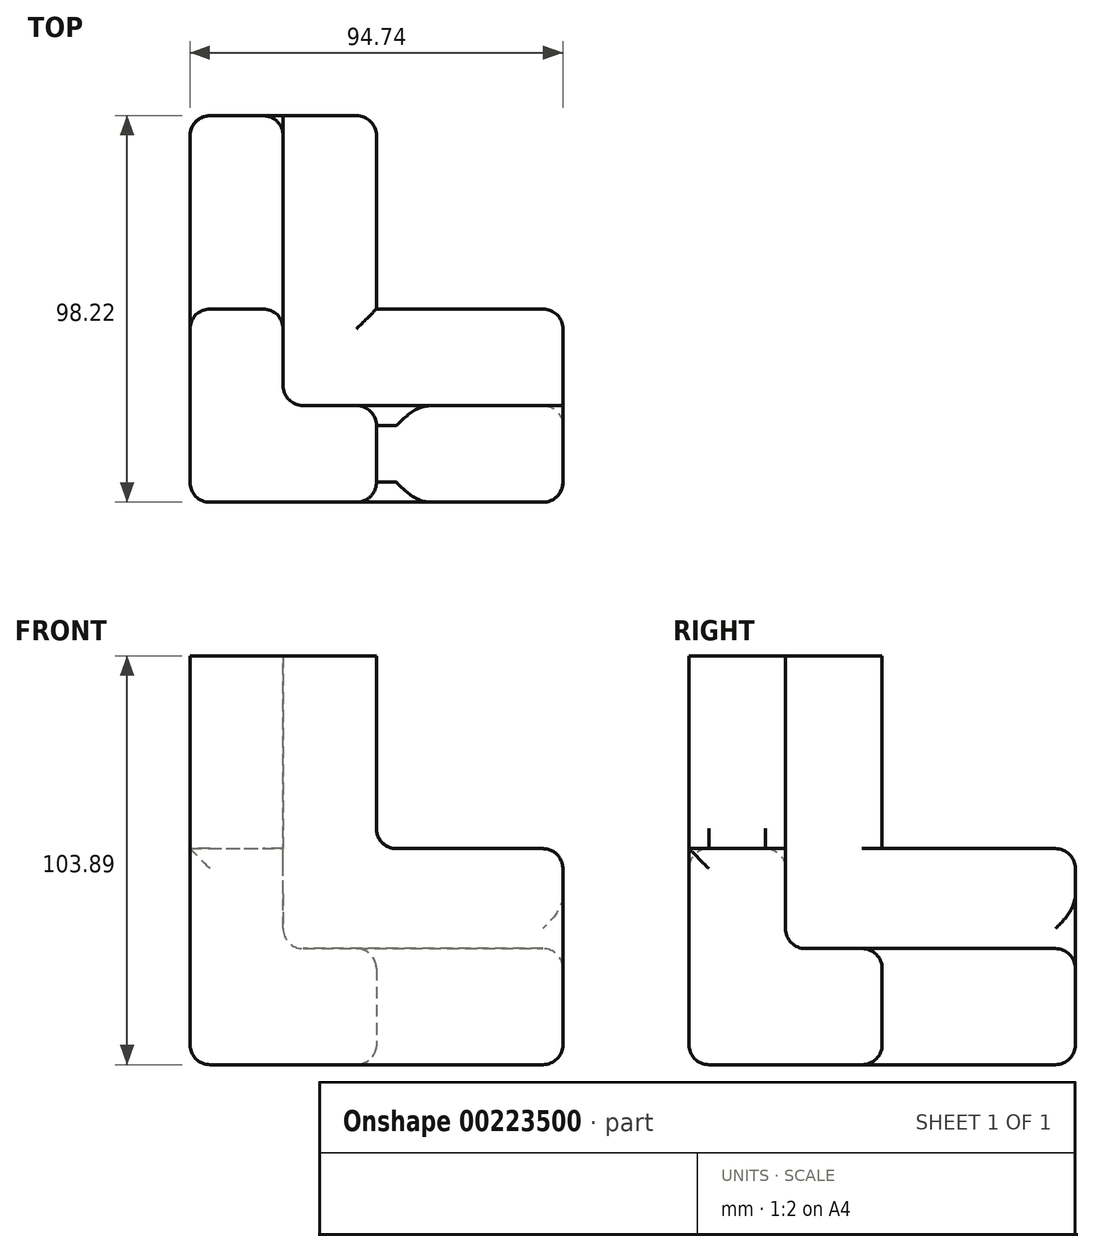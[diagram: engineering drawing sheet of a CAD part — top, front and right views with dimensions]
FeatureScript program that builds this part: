
annotation { "Feature Type Name" : "Feature", "Feature Type Description" : "" }
export const myFeature = defineFeature(function(context is Context, id is Id, definition is map)
    precondition{}
    {
        {
            var Q0;
            Q0=qCreatedBy(makeId("Top.planeOp"),FACE);
            var sketch = newSketch(context, id + "F6", { "sketchPlane" : qUnion([Q0])});
            skLineSegment(sketch, "E0.bottom", {"start": v(-47.37, -49.1) * mm, "end": v(47.37, -49.1) * mm});
            skLineSegment(sketch, "E0.top", {"start": v(-47.37, 49.1) * mm, "end": v(47.37, 49.1) * mm});
            skLineSegment(sketch, "E0.left", {"start": v(-47.37, -49.1) * mm, "end": v(-47.37, 49.1) * mm});
            skLineSegment(sketch, "E0.right", {"start": v(47.37, -49.1) * mm, "end": v(47.37, 49.1) * mm});
            skPoint(sketch, "E0.middle", {"position": v(0, 0) * mm});
            skLineSegment(sketch, "E1.bottom", {"start": v(75.08, 68.47) * mm, "end": v(75.34, 68.47) * mm});
            skLineSegment(sketch, "E1.top", {"start": v(75.08, 73.74) * mm, "end": v(75.34, 73.74) * mm});
            skLineSegment(sketch, "E1.left", {"start": v(75.08, 68.47) * mm, "end": v(75.08, 73.74) * mm});
            skLineSegment(sketch, "E1.right", {"start": v(75.34, 68.47) * mm, "end": v(75.34, 73.74) * mm});
            skPoint(sketch, "E1.middle", {"position": v(75.2, 71.1) * mm});
            skLineSegment(sketch, "E2.bottom", {"start": v(0, 0) * mm, "end": v(94.75, 0) * mm});
            skLineSegment(sketch, "E2.top", {"start": v(0, 98.21) * mm, "end": v(94.75, 98.21) * mm});
            skLineSegment(sketch, "E2.left", {"start": v(0, 0) * mm, "end": v(0, 98.21) * mm});
            skLineSegment(sketch, "E2.right", {"start": v(94.75, 0) * mm, "end": v(94.75, 98.21) * mm});
            skPoint(sketch, "E2.middle", {"position": v(47.37, 49.1) * mm});
            skSolve(sketch);
        }
        {
            var Q0;
            {var subQ1=sQuery(id+"F6.wireOp",EDGE,"E0.bottom");Q0=makeQuery(id+"F6.imprint","IMPRINT",FACE,{"disambiguationData":[TD([[makeQuery(id+"F6.imprint","IMPRINT",EDGE,{"derivedFrom":subQ1}),1.0]])]});}
            var sketch = newSketch(context, id + "F7", { "sketchPlane" : qUnion([Q0])});
            skSolve(sketch);
        }
        {
            var Q0;
            Q0 = qSketchRegion(id + "F7", true);
            var Q1;
            {var subQ1=sQuery(id+"F6.wireOp",EDGE,"E0.bottom");Q1=makeQuery(id+"F6.imprint","IMPRINT",FACE,{"disambiguationData":[TD([[makeQuery(id+"F6.imprint","IMPRINT",EDGE,{"derivedFrom":subQ1}),1.0]])]});}
            extrude(context, id + "F8", {"entities" : qUnion([Q0, Q1]), "depth" : 54.9 * mm});
        }
        {
            var Q0;
            Q0=makeQuery(id+"F8.opExtrude","CAP_FACE",FACE,{"disambiguationData":[OSD([sQuery(id+"F6.wireOp",EDGE,"E0.bottom"),sQuery(id+"F6.wireOp",EDGE,"E0.top"),sQuery(id+"F6.wireOp",EDGE,"E0.left"),sQuery(id+"F6.wireOp",EDGE,"E0.right"),sQuery(id+"F6.wireOp",EDGE,"E2.bottom"),sQuery(id+"F6.wireOp",EDGE,"E2.left")])],"isStart":false});
            var sketch = newSketch(context, id + "F0", { "sketchPlane" : qUnion([Q0])});
            skLineSegment(sketch, "E3", {"start": v(-23.69, 49.1) * mm, "end": v(-23.69, -24.55) * mm});
            skPoint(sketch, "E3.endSnap0", {"position": v(47.37, -24.55) * mm});
            skLineSegment(sketch, "E4", {"start": v(-23.69, -24.55) * mm, "end": v(47.37, -24.55) * mm});
            skSolve(sketch);
        }
        {
            var Q0;
            {var subQ1=sQuery(id+"F0.wireOp",EDGE,"E3");Q0=makeQuery(id+"F0.imprint","IMPRINT",FACE,{"disambiguationData":[TD([[makeQuery(id+"F0.imprint","IMPRINT",EDGE,{"derivedFrom":subQ1}),1.0]])]});}
            extrude(context, id + "F1", {"entities" : qUnion([Q0]), "operationType" : NewBodyOperationType.ADD, "oppositeDirection" : true, "depth" : 36.75 * mm});
        }
        {
            var Q0;
            Q0=makeQuery(id+"F8.opExtrude","CAP_FACE",FACE,{"disambiguationData":[OSD([sQuery(id+"F6.wireOp",EDGE,"E0.bottom"),sQuery(id+"F6.wireOp",EDGE,"E0.top"),sQuery(id+"F6.wireOp",EDGE,"E0.left"),sQuery(id+"F6.wireOp",EDGE,"E0.right"),sQuery(id+"F6.wireOp",EDGE,"E2.bottom"),sQuery(id+"F6.wireOp",EDGE,"E2.left")])],"isStart":false});
            var sketch = newSketch(context, id + "F2", { "sketchPlane" : qUnion([Q0])});
            skLineSegment(sketch, "E5", {"start": v(47.37, -24.55) * mm, "end": v(-23.69, -24.55) * mm});
            skPoint(sketch, "E5.endSnap0", {"position": v(-23.69, 49.1) * mm});
            skLineSegment(sketch, "E6", {"start": v(-23.69, -24.55) * mm, "end": v(-23.69, 49.1) * mm});
            skSolve(sketch);
        }
        {
            var Q0;
            {var subQ3=sQuery(id+"F2.wireOp",EDGE,"E5");Q0=makeQuery(id+"F2.imprint","IMPRINT",FACE,{"disambiguationData":[TD([[makeQuery(id+"F2.imprint","IMPRINT",EDGE,{"derivedFrom":subQ3}),-1.0]])]});}
            extrude(context, id + "F3", {"entities" : qUnion([Q0]), "operationType" : NewBodyOperationType.REMOVE, "oppositeDirection" : true, "depth" : 25.4 * mm});
        }
        {
            var Q0;
            Q0=makeQuery(id+"F8.opExtrude","CAP_FACE",FACE,{"disambiguationData":[OSD([sQuery(id+"F6.wireOp",EDGE,"E0.bottom"),sQuery(id+"F6.wireOp",EDGE,"E0.top"),sQuery(id+"F6.wireOp",EDGE,"E0.left"),sQuery(id+"F6.wireOp",EDGE,"E0.right"),sQuery(id+"F6.wireOp",EDGE,"E2.bottom"),sQuery(id+"F6.wireOp",EDGE,"E2.left")])],"isStart":false});
            var sketch = newSketch(context, id + "F9", { "sketchPlane" : qUnion([Q0])});
            skLineSegment(sketch, "E7", {"start": v(-0.01, -24.55) * mm, "end": v(0, -49.1) * mm});
            skLineSegment(sketch, "E8", {"start": v(0, -49.1) * mm, "end": v(-47.37, -49.1) * mm});
            skLineSegment(sketch, "E9", {"start": v(-47.37, -11.88) * mm, "end": v(-47.37, -49.1) * mm});
            skLineSegment(sketch, "E10", {"start": v(-23.69, -19.02) * mm, "end": v(-23.69, 0) * mm});
            skLineSegment(sketch, "E11", {"start": v(-23.69, 0) * mm, "end": v(-23.69, 0) * mm});
            skLineSegment(sketch, "E12", {"start": v(-47.37, 0) * mm, "end": v(-23.69, 0) * mm});
            skSolve(sketch);
        }
        {
            var Q0;
            {var subQ5=sQuery(id+"F9.wireOp",EDGE,"E7");Q0=makeQuery(id+"F9.imprint","IMPRINT",FACE,{"disambiguationData":[TD([[makeQuery(id+"F9.imprint","IMPRINT",EDGE,{"derivedFrom":subQ5}),-1.0]])]});}
            extrude(context, id + "F10", {"entities" : qUnion([Q0]), "operationType" : NewBodyOperationType.ADD, "depth" : 62.18 * mm});
        }
        {
            var Q0;
            Q0=makeQuery(id+"F10.opExtrude","CAP_FACE",FACE,{"disambiguationData":[OSD([sQuery(id+"F6.wireOp",EDGE,"E0.left"),sQuery(id+"F2.wireOp",EDGE,"E5"),sQuery(id+"F2.wireOp",EDGE,"E6"),sQuery(id+"F9.wireOp",EDGE,"E7"),sQuery(id+"F9.wireOp",EDGE,"E8"),sQuery(id+"F9.wireOp",EDGE,"E9"),sQuery(id+"F9.wireOp",EDGE,"E10"),sQuery(id+"F9.wireOp",EDGE,"E12")])],"isStart":false});
            extrude(context, id + "F4", {"entities" : qUnion([Q0]), "operationType" : NewBodyOperationType.REMOVE, "oppositeDirection" : true, "depth" : 13.18 * mm});
        }
        {
            var Q0;
            Q0=makeQuery(id+"F4.boolean.opBoolean","COPY",EDGE,{"derivedFrom":makeQuery(id+"F4.opExtrude","CAP_EDGE",EDGE,{"disambiguationData":[OSD([sQuery(id+"F9.wireOp",EDGE,"E7")])],"isStart":false})});
            var Q1;
            {var subQ0=sQuery(id+"F2.wireOp",EDGE,"E6");var subQ1=sQuery(id+"F2.wireOp",EDGE,"E5");Q1=makeQuery(id+"F10.boolean.opBoolean","MERGE",EDGE,{"derivedFrom":[makeQuery(id+"F3.boolean.opBoolean","COPY",EDGE,{"derivedFrom":makeQuery(id+"F3.opExtrude","SWEPT_EDGE",EDGE,{"disambiguationData":[OSD([subQ1,subQ0])]})}),makeQuery(id+"F10.opExtrude","SWEPT_EDGE",EDGE,{"disambiguationData":[OSD([subQ1,subQ0])]})]});}
            var Q2;
            Q2=makeQuery(id+"F4.boolean.opBoolean","COPY",EDGE,{"derivedFrom":makeQuery(id+"F4.opExtrude","CAP_EDGE",EDGE,{"disambiguationData":[OSD([sQuery(id+"F2.wireOp",EDGE,"E5")])],"isStart":false})});
            var Q3;
            Q3=makeQuery(id+"F4.boolean.opBoolean","COPY",EDGE,{"derivedFrom":makeQuery(id+"F4.opExtrude","CAP_EDGE",EDGE,{"disambiguationData":[OSD([sQuery(id+"F2.wireOp",EDGE,"E6"),sQuery(id+"F9.wireOp",EDGE,"E10")])],"isStart":false})});
            var Q4;
            Q4=makeQuery(id+"F4.boolean.opBoolean","COPY",EDGE,{"derivedFrom":makeQuery(id+"F4.opExtrude","CAP_EDGE",EDGE,{"disambiguationData":[OSD([sQuery(id+"F9.wireOp",EDGE,"E12")])],"isStart":false})});
            var Q5;
            Q5=makeQuery(id+"F4.boolean.opBoolean","COPY",EDGE,{"derivedFrom":makeQuery(id+"F4.opExtrude","CAP_EDGE",EDGE,{"disambiguationData":[OSD([sQuery(id+"F6.wireOp",EDGE,"E0.left"),sQuery(id+"F9.wireOp",EDGE,"E9")])],"isStart":false})});
            var Q6;
            Q6=makeQuery(id+"F4.boolean.opBoolean","COPY",EDGE,{"derivedFrom":makeQuery(id+"F4.opExtrude","CAP_EDGE",EDGE,{"disambiguationData":[OSD([sQuery(id+"F9.wireOp",EDGE,"E8")])],"isStart":false})});
            var Q7;
            Q7=makeQuery(id+"F10.opExtrude","SWEPT_EDGE",EDGE,{"disambiguationData":[OSD([sQuery(id+"F2.wireOp",EDGE,"E5"),sQuery(id+"F9.wireOp",EDGE,"E7")])]});
            var Q8;
            Q8=makeQuery(id+"F10.opExtrude","SWEPT_EDGE",EDGE,{"disambiguationData":[OSD([sQuery(id+"F6.wireOp",EDGE,"E0.bottom"),sQuery(id+"F9.wireOp",EDGE,"E7"),sQuery(id+"F9.wireOp",EDGE,"E8")])]});
            var Q9;
            Q9=makeQuery(id+"F10.opExtrude","SWEPT_EDGE",EDGE,{"disambiguationData":[OSD([sQuery(id+"F2.wireOp",EDGE,"E6"),sQuery(id+"F9.wireOp",EDGE,"E10"),sQuery(id+"F9.wireOp",EDGE,"E12")])]});
            var Q10;
            Q10=makeQuery(id+"F10.opExtrude","SWEPT_EDGE",EDGE,{"disambiguationData":[OSD([sQuery(id+"F6.wireOp",EDGE,"E0.left"),sQuery(id+"F9.wireOp",EDGE,"E12")])]});
            var Q11;
            Q11=makeQuery(id+"F10.opExtrude","CAP_EDGE",EDGE,{"disambiguationData":[OSD([sQuery(id+"F9.wireOp",EDGE,"E12")])],"isStart":true});
            var Q12;
            Q12=makeQuery(id+"F10.opExtrude","CAP_EDGE",EDGE,{"disambiguationData":[OSD([sQuery(id+"F9.wireOp",EDGE,"E7")])],"isStart":true});
            var Q13;
            Q13=makeQuery(id+"F8.opExtrude","CAP_EDGE",EDGE,{"disambiguationData":[OSD([sQuery(id+"F6.wireOp",EDGE,"E0.right")])],"isStart":false});
            var Q14;
            Q14=makeQuery(id+"F8.opExtrude","CAP_EDGE",EDGE,{"disambiguationData":[OSD([sQuery(id+"F6.wireOp",EDGE,"E0.top")])],"isStart":false});
            var Q15;
            Q15=makeQuery(id+"F8.opExtrude","CAP_EDGE",EDGE,{"disambiguationData":[OSD([sQuery(id+"F6.wireOp",EDGE,"E2.bottom")])],"isStart":true});
            var Q16;
            Q16=makeQuery(id+"F8.opExtrude","CAP_EDGE",EDGE,{"disambiguationData":[OSD([sQuery(id+"F6.wireOp",EDGE,"E0.right")])],"isStart":true});
            var Q17;
            Q17=makeQuery(id+"F8.opExtrude","SWEPT_EDGE",EDGE,{"disambiguationData":[OSD([sQuery(id+"F6.wireOp",EDGE,"E0.right"),sQuery(id+"F6.wireOp",EDGE,"E2.bottom")])]});
            var Q18;
            Q18=makeQuery(id+"F3.boolean.opBoolean","COPY",EDGE,{"derivedFrom":makeQuery(id+"F3.opExtrude","CAP_EDGE",EDGE,{"disambiguationData":[OSD([sQuery(id+"F6.wireOp",EDGE,"E2.bottom")])],"isStart":false})});
            var Q19;
            Q19=makeQuery(id+"F3.boolean.opBoolean","COPY",EDGE,{"derivedFrom":makeQuery(id+"F3.opExtrude","CAP_EDGE",EDGE,{"disambiguationData":[OSD([sQuery(id+"F6.wireOp",EDGE,"E0.right")])],"isStart":false})});
            var Q20;
            Q20=makeQuery(id+"F3.boolean.opBoolean","COPY",FACE,{"derivedFrom":makeQuery(id+"F3.opExtrude","CAP_FACE",FACE,{"disambiguationData":[OSD([sQuery(id+"F6.wireOp",EDGE,"E0.top"),sQuery(id+"F6.wireOp",EDGE,"E0.right"),sQuery(id+"F6.wireOp",EDGE,"E2.bottom"),sQuery(id+"F6.wireOp",EDGE,"E2.left"),sQuery(id+"F2.wireOp",EDGE,"E5"),sQuery(id+"F2.wireOp",EDGE,"E6")])],"isStart":false})});
            var Q21;
            Q21=makeQuery(id+"F8.opExtrude","SWEPT_EDGE",EDGE,{"disambiguationData":[OSD([sQuery(id+"F6.wireOp",EDGE,"E0.top"),sQuery(id+"F6.wireOp",EDGE,"E2.left")])]});
            var Q22;
            Q22=makeQuery(id+"F8.opExtrude","CAP_EDGE",EDGE,{"disambiguationData":[OSD([sQuery(id+"F6.wireOp",EDGE,"E2.left")])],"isStart":true});
            var Q23;
            Q23=makeQuery(id+"F8.opExtrude","SWEPT_EDGE",EDGE,{"disambiguationData":[OSD([sQuery(id+"F6.wireOp",EDGE,"E0.bottom"),sQuery(id+"F6.wireOp",EDGE,"E0.right")])]});
            var Q24;
            Q24=makeQuery(id+"F8.opExtrude","CAP_EDGE",EDGE,{"disambiguationData":[OSD([sQuery(id+"F6.wireOp",EDGE,"E0.bottom")])],"isStart":true});
            var Q25;
            Q25=makeQuery(id+"F10.boolean.opBoolean","MERGE",EDGE,{"derivedFrom":[makeQuery(id+"F8.opExtrude","SWEPT_EDGE",EDGE,{"disambiguationData":[OSD([sQuery(id+"F6.wireOp",EDGE,"E0.bottom"),sQuery(id+"F6.wireOp",EDGE,"E0.left")])]}),makeQuery(id+"F10.opExtrude","SWEPT_EDGE",EDGE,{"disambiguationData":[OSD([sQuery(id+"F9.wireOp",EDGE,"E8"),sQuery(id+"F9.wireOp",EDGE,"E9")])]})]});
            var Q26;
            Q26=makeQuery(id+"F8.opExtrude","CAP_EDGE",EDGE,{"disambiguationData":[OSD([sQuery(id+"F6.wireOp",EDGE,"E0.top")])],"isStart":true});
            var Q27;
            Q27=makeQuery(id+"F8.opExtrude","SWEPT_EDGE",EDGE,{"disambiguationData":[OSD([sQuery(id+"F6.wireOp",EDGE,"E0.top"),sQuery(id+"F6.wireOp",EDGE,"E0.left")])]});
            var Q28;
            Q28=makeQuery(id+"F8.opExtrude","CAP_EDGE",EDGE,{"disambiguationData":[OSD([sQuery(id+"F6.wireOp",EDGE,"E0.left")])],"isStart":true});
            fillet(context, id + "F5", {"entities" : qUnion([Q0, Q1, Q2, Q3, Q4, Q5, Q6, Q7, Q8, Q9, Q10, Q11, Q12, Q13, Q14, Q15, Q16, Q17, Q18, Q19, Q20, Q21, Q22, Q23, Q24, Q25, Q26, Q27, Q28]), "radius" : 5.08 * mm, "tangentPropagation" : true, "allowEdgeOverflow" : false});
        }
    });
